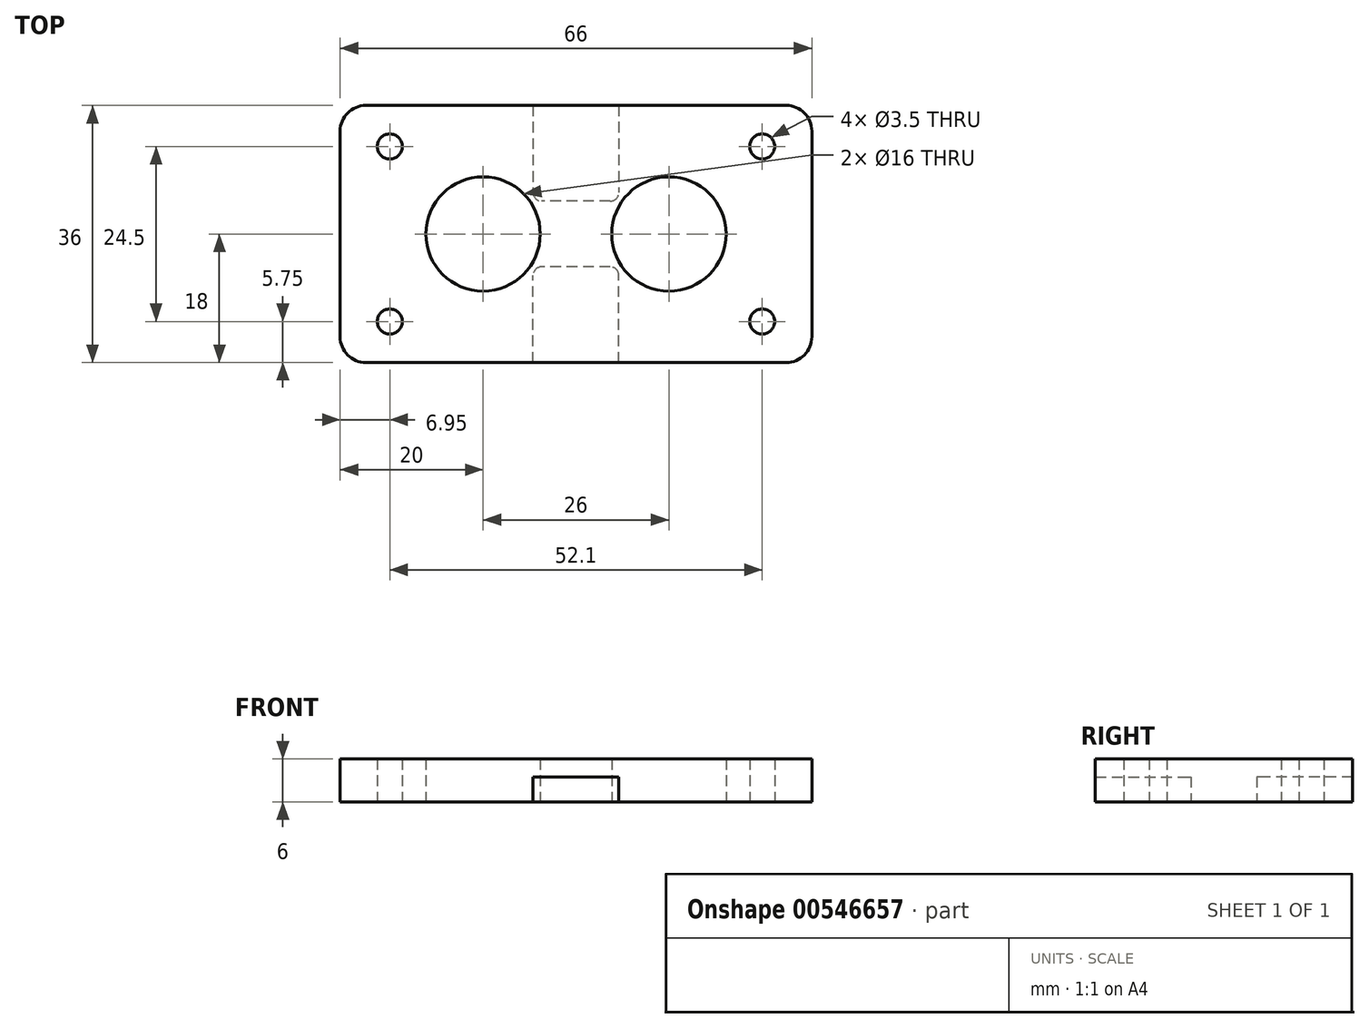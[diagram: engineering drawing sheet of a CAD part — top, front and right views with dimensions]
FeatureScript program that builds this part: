
annotation { "Feature Type Name" : "Feature", "Feature Type Description" : "" }
export const myFeature = defineFeature(function(context is Context, id is Id, definition is map)
    precondition{}
    {
        {
            var Q0;
            Q0=qCreatedBy(makeId("Top.planeOp"),FACE);
            var sketch = newSketch(context, id + "F0", { "sketchPlane" : qUnion([Q0])});
            skLineSegment(sketch, "E0.bottom", {"start": v(29.4, 18) * mm, "end": v(-29.4, 18) * mm});
            skLineSegment(sketch, "E0.top", {"start": v(29.4, -18) * mm, "end": v(-29.4, -18) * mm});
            skLineSegment(sketch, "E0.left", {"start": v(33, 14.4) * mm, "end": v(33, -14.4) * mm});
            skLineSegment(sketch, "E0.right", {"start": v(-33, 14.4) * mm, "end": v(-33, -14.4) * mm});
            skPoint(sketch, "E0.middle", {"position": v(0, 0) * mm});
            skCircle(sketch, "E1", {"center": v(-13, 0) * mm, "radius": 8 * mm});
            skCircle(sketch, "E2.MirrorC", {"center": v(13, 0) * mm, "radius": 8 * mm});
            skCircle(sketch, "E3", {"center": v(-26.05, 12.25) * mm, "radius": 1.75 * mm});
            skCircle(sketch, "E4.MirrorC", {"center": v(26.05, 12.25) * mm, "radius": 1.75 * mm});
            skCircle(sketch, "E5.MirrorC", {"center": v(26.05, -12.25) * mm, "radius": 1.75 * mm});
            skCircle(sketch, "E6.MirrorC", {"center": v(-26.05, -12.25) * mm, "radius": 1.75 * mm});
            skPoint(sketch, "E7.visualSharp", {"position": v(-33, 18) * mm});
            skArc(sketch, "E7.filletArc", {"start": v(-29.4, 18) * mm, "mid": v(-31.95, 16.95) * mm, "end": v(-33, 14.4) * mm});
            skPoint(sketch, "E8.visualSharp", {"position": v(33, 18) * mm});
            skArc(sketch, "E8.filletArc", {"start": v(33, 14.4) * mm, "mid": v(31.95, 16.95) * mm, "end": v(29.4, 18) * mm});
            skPoint(sketch, "E9.visualSharp", {"position": v(33, -18) * mm});
            skArc(sketch, "E9.filletArc", {"start": v(29.4, -18) * mm, "mid": v(31.95, -16.95) * mm, "end": v(33, -14.4) * mm});
            skPoint(sketch, "E10.visualSharp", {"position": v(-33, -18) * mm});
            skArc(sketch, "E10.filletArc", {"start": v(-33, -14.4) * mm, "mid": v(-31.95, -16.95) * mm, "end": v(-29.4, -18) * mm});
            skSolve(sketch);
        }
        {
            var Q0;
            Q0 = qSketchRegion(id + "F0", true);
            extrude(context, id + "F1", {"entities" : qUnion([Q0]), "depth" : 6 * mm, "offsetDistance" : 25 * mm});
        }
        {
            var Q0;
            Q0=makeQuery(id+"F0.imprint","IMPRINT",FACE,{"disambiguationData":[TD([[makeQuery(id+"F0.imprint","IMPRINT",EDGE,{"derivedFrom":sQuery(id+"F0.wireOp",EDGE,"E0.bottom")}),1.0]])]});
            var sketch = newSketch(context, id + "F2", { "sketchPlane" : qUnion([Q0])});
            skLineSegment(sketch, "E11.bottom", {"start": v(6, -18) * mm, "end": v(-6, -18) * mm});
            skLineSegment(sketch, "E11.top", {"start": v(4.8, -4.6) * mm, "end": v(-4.8, -4.6) * mm});
            skLineSegment(sketch, "E11.left", {"start": v(6, -18) * mm, "end": v(6, -5.8) * mm});
            skLineSegment(sketch, "E11.right", {"start": v(-6, -18) * mm, "end": v(-6, -5.8) * mm});
            skPoint(sketch, "E11.middle", {"position": v(0, -11.3) * mm});
            skPoint(sketch, "E12.visualSharp", {"position": v(-6, -4.6) * mm});
            skArc(sketch, "E12.filletArc", {"start": v(-4.8, -4.6) * mm, "mid": v(-5.65, -4.95) * mm, "end": v(-6, -5.8) * mm});
            skPoint(sketch, "E13.visualSharp", {"position": v(6, -4.6) * mm});
            skArc(sketch, "E13.filletArc", {"start": v(6, -5.8) * mm, "mid": v(5.65, -4.95) * mm, "end": v(4.8, -4.6) * mm});
            skArc(sketch, "E14.MirrorCS", {"start": v(6, 5.8) * mm, "mid": v(5.65, 4.95) * mm, "end": v(4.8, 4.6) * mm});
            skArc(sketch, "E15.MirrorCS", {"start": v(-4.8, 4.6) * mm, "mid": v(-5.65, 4.95) * mm, "end": v(-6, 5.8) * mm});
            skPoint(sketch, "E16.MirrorP", {"position": v(0, 11.3) * mm});
            skLineSegment(sketch, "E17.MirrorCS", {"start": v(4.8, 4.6) * mm, "end": v(-4.8, 4.6) * mm});
            skLineSegment(sketch, "E18.MirrorCS", {"start": v(-6, 18) * mm, "end": v(-6, 5.8) * mm});
            skLineSegment(sketch, "E19.MirrorCS", {"start": v(6, 18) * mm, "end": v(-6, 18) * mm});
            skPoint(sketch, "E20.MirrorP", {"position": v(6, 4.6) * mm});
            skLineSegment(sketch, "E21.MirrorCS", {"start": v(6, 18) * mm, "end": v(6, 5.8) * mm});
            skPoint(sketch, "E22.MirrorP", {"position": v(-6, 4.6) * mm});
            skSolve(sketch);
        }
        {
            var Q0;
            Q0 = qSketchRegion(id + "F2", true);
            extrude(context, id + "F3", {"entities" : qUnion([Q0]), "operationType" : NewBodyOperationType.REMOVE, "depth" : 3.5 * mm, "offsetDistance" : 25 * mm});
        }
    });
